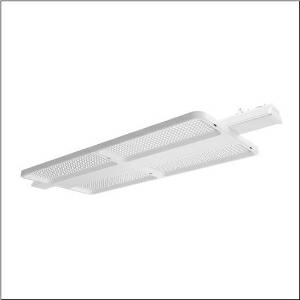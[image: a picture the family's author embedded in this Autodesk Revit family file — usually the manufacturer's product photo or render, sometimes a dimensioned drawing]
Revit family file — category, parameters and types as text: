
# Revit family: highbay_21_fur_licross_tragschiene_maxi_52hn11db3lla
name_source: partatom
category: Lighting Fixtures
units: mm (PartAtom-declared; Revit-internal decimal feet)

## family parameters
Cut with Voids When Loaded = No
Host = Face
Light Source = No
Part Type = Normal
Room Calculation Point = No
Round Connector Dimension = Use Diameter
Shared = No

## types (1)
- --- (1 x LED, 3880 lm, 22.6 W, 3000K)
    Apparent Load = 23 VA
    CIE Flux Codes = 89 97 99 100 100
    Color Rendering = 80
    Color Temperature = 3000K
    Default Elevation = 1800 mm
    Description = high bay luminaire Highbay 21 for Licross trunking rail maxi; direct symmetric narrow distribution, light control with lens of PMMA; UGR ≤ 19 (X = 4H | Y = 8H | S = 0.25H | reflection values 70/50/20); luminous flux: 25.590lm; light colour: 830, colour temperature: 3000K, MacAdam ≤ 3 SDCM (initial), colour rendering: CRI > 80; luminous efficacy: 177,7lm/W; rated service life: 75.000h (L80) at AT= ta max; control: DALI 2; luminaire connection: plug, 5-pole, with phase selectionmains connection: 230..240V, AC 50/60Hz; connected load: 144W; protection rating (complete): IP64; insulation class (complete): insulation class I (protective earthing); protection symbol: D; impact resistance: IK06; certification: CE, ENEC, VDE, UKCA; internal wiring halogen-free; luminaire LABS conformity tested according to VDMA 24364:2018-05; Suitable for use in the food industry according to the specifications of IFS-Food, HACCP and/or BRC; housing frame of high-performance plastic PA6, matt traffic white (RAL 9016); cover of PMMA; fixing on rail side of steel, galvanised, white; blank cover of PC/ABS, traffic white (RAL 9016); dimension (LxWxH): 1.250 x 442 x 71mm; permissible operating ambient temperature: -40..+55°C (reducing of maximum allowable ambient temperature of 5°C with ceiling mounting); packaging unit: 1 piece
    Height = 72 mm  [stored 0.23622 ft]
    Lamp = 1 x LED
    Lamp Light Flux = 3880 lm
    Lamp Power = 22.6 W
    Lamp count = 1
    Length = 946 mm
    Luminous efficacy = 172 lm/W
    Manufacturer = Siteco
    ModVariant = No
    Model = 52HN11DB3LLA
    Mounting Place = Ceiling
    Mounting Type = Pendant
    Number of Poles = 1
    OnlyDefault = Yes
    Power Factor = 1
    Product Name = Highbay 21 für Licross Tragschiene maxi
    Product group = high bay luminaire
    ProductGroupID = 902
    Protection Class = Protection class I
    Protection Degree = IP 64
    RLX_Detail_Level = 1
    RLX_Emergency_Light_Flux = 0 lm
    RLX_Emergency_Type = 0
    RLX_Emergency_Type_DB = No
    RlxData = <blob elided: 130705 chars, md5=37b96e7d>
    Socket = socket
    Standby Power = 0 W
    System Light Flux = 3880 lm
    System Power = 23 W
    Type Comments = : DC mode (central or group accumulator) initial emergency light level
    Type Image = l_1361711.jpg
    URL = http://relux.com
    VarID = @adj_001731
    Voltage = 0 V
    Weight = 0.00 kg
    Width = 442 mm

note: [stored X ft] marks values corroborated as IEEE doubles in the binary element streams (Revit-internal decimal feet)

## geometry (parser evidence)
native form markers: Blend x4, Sweep x10
no freeform markers — native parametric forms only
